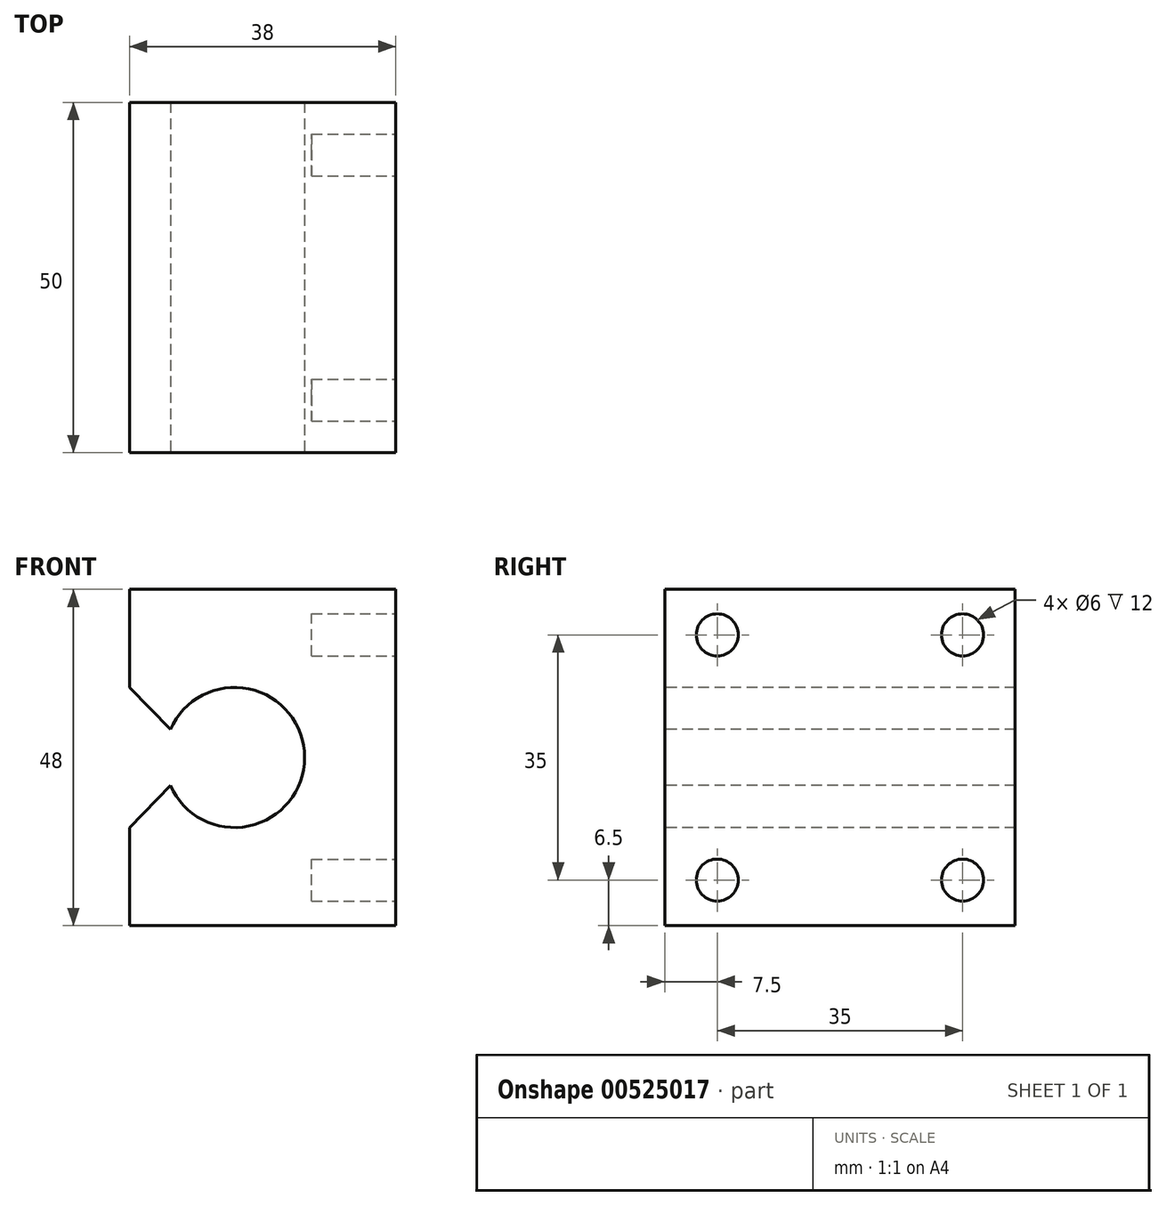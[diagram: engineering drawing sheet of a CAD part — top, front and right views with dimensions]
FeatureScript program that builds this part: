
annotation { "Feature Type Name" : "Feature", "Feature Type Description" : "" }
export const myFeature = defineFeature(function(context is Context, id is Id, definition is map)
    precondition{}
    {
        {
            var Q0;
            Q0=qCreatedBy(makeId("Front.planeOp"),FACE);
            var sketch = newSketch(context, id + "F0", { "sketchPlane" : qUnion([Q0])});
            skLineSegment(sketch, "E0.bottom", {"start": v(0, -24) * mm, "end": v(38, -24) * mm});
            skLineSegment(sketch, "E0.top", {"start": v(0, 24) * mm, "end": v(38, 24) * mm});
            skLineSegment(sketch, "E0.left", {"start": v(0, -24) * mm, "end": v(0, 24) * mm});
            skLineSegment(sketch, "E0.right", {"start": v(38, -24) * mm, "end": v(38, 24) * mm});
            skSolve(sketch);
        }
        {
            var Q0;
            Q0 = qSketchRegion(id + "F0", true);
            extrude(context, id + "F1", {"entities" : qUnion([Q0]), "endBound" : BoundingType.SYMMETRIC, "depth" : 50 * mm, "offsetDistance" : 25 * mm});
        }
        {
            var Q0;
            Q0=makeQuery(id+"F1.opExtrude","CAP_FACE",FACE,{"disambiguationData":[OSD([sQuery(id+"F0.wireOp",EDGE,"E0.bottom"),sQuery(id+"F0.wireOp",EDGE,"E0.top"),sQuery(id+"F0.wireOp",EDGE,"E0.left"),sQuery(id+"F0.wireOp",EDGE,"E0.right")])],"isStart":false});
            var sketch = newSketch(context, id + "F2", { "sketchPlane" : qUnion([Q0])});
            skArc(sketch, "E1", {"start": v(5.83, -4) * mm, "mid": v(25, 0) * mm, "end": v(5.83, 4) * mm});
            skLineSegment(sketch, "E2", {"start": v(0, 10) * mm, "end": v(5.83, 4) * mm});
            skLineSegment(sketch, "E3", {"start": v(5.83, -4) * mm, "end": v(0, -10) * mm});
            skLineSegment(sketch, "E4", {"start": v(0, 10) * mm, "end": v(0, -10) * mm});
            skSolve(sketch);
        }
        {
            var Q0;
            Q0 = qSketchRegion(id + "F2", true);
            extrude(context, id + "F3", {"entities" : qUnion([Q0]), "operationType" : NewBodyOperationType.REMOVE, "oppositeDirection" : true, "depth" : 50 * mm, "offsetDistance" : 25 * mm});
        }
        {
            var Q0;
            Q0=makeQuery(id+"F1.opExtrude","SWEPT_FACE",FACE,{"disambiguationData":[OSD([sQuery(id+"F0.wireOp",EDGE,"E0.right")])]});
            var sketch = newSketch(context, id + "F4", { "sketchPlane" : qUnion([Q0])});
            skCircle(sketch, "E5", {"center": v(-17.5, 17.5) * mm, "radius": 3 * mm});
            skCircle(sketch, "E6", {"center": v(17.5, 17.5) * mm, "radius": 3 * mm});
            skCircle(sketch, "E7", {"center": v(17.5, -17.5) * mm, "radius": 3 * mm});
            skCircle(sketch, "E8", {"center": v(-17.5, -17.5) * mm, "radius": 3 * mm});
            skSolve(sketch);
        }
        {
            var Q0;
            Q0 = qSketchRegion(id + "F4", true);
            extrude(context, id + "F5", {"entities" : qUnion([Q0]), "operationType" : NewBodyOperationType.REMOVE, "oppositeDirection" : true, "depth" : 12 * mm, "offsetDistance" : 25 * mm});
        }
    });
